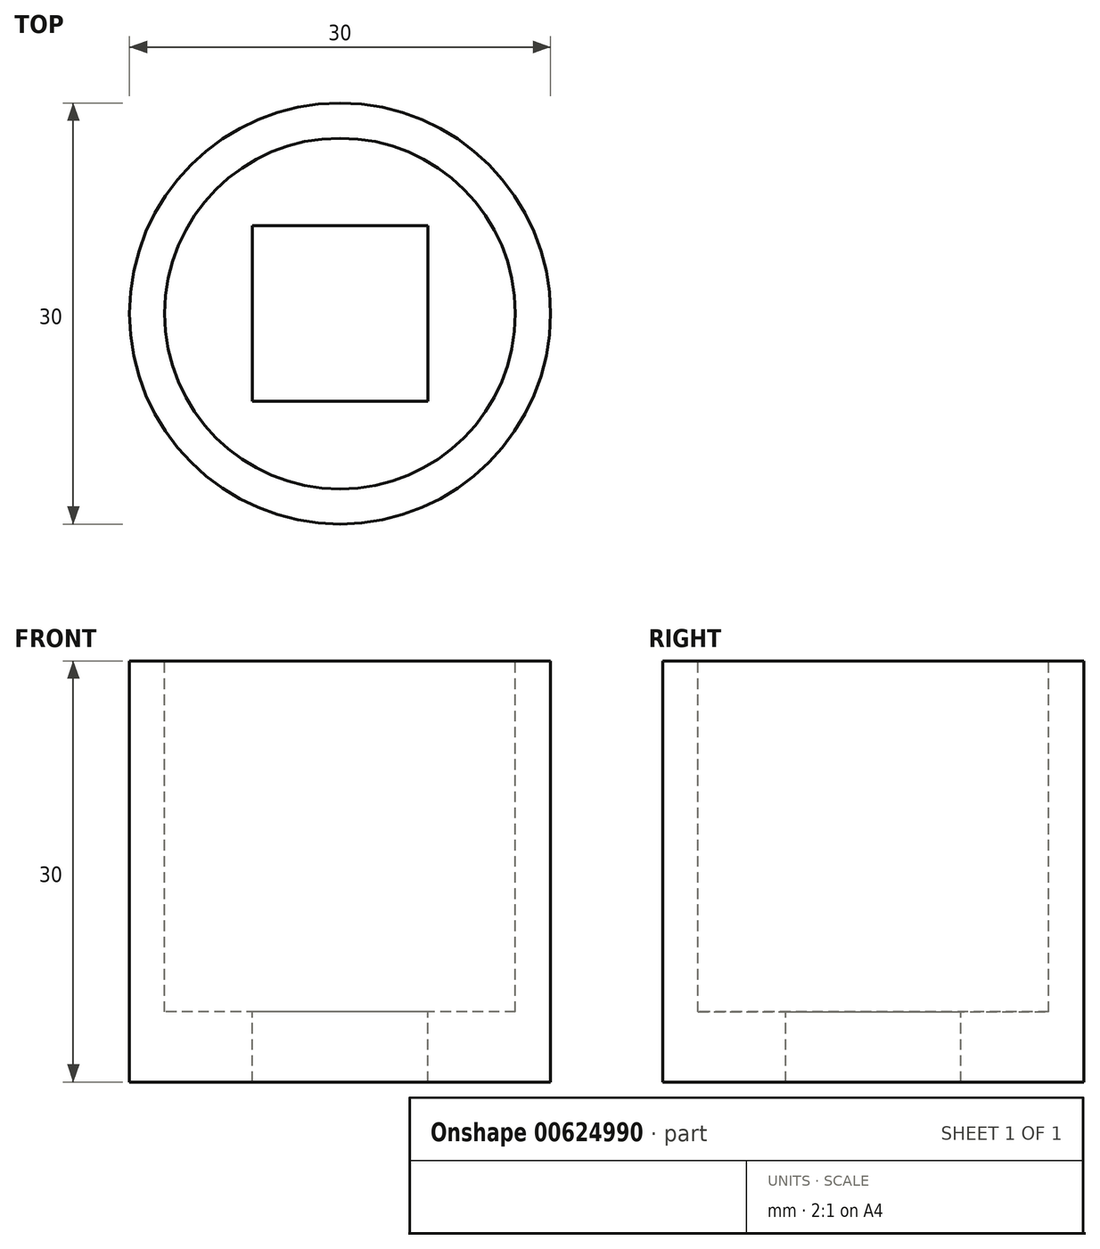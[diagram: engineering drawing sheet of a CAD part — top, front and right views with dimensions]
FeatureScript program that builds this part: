
annotation { "Feature Type Name" : "Feature", "Feature Type Description" : "" }
export const myFeature = defineFeature(function(context is Context, id is Id, definition is map)
    precondition{}
    {
        {
            var Q0;
            Q0=qCreatedBy(makeId("Top.planeOp"),FACE);
            var sketch = newSketch(context, id + "F0", { "sketchPlane" : qUnion([Q0])});
            skCircle(sketch, "E0", {"center": v(0, 0) * mm, "radius": 15 * mm});
            skSolve(sketch);
        }
        {
            var Q0;
            Q0=makeQuery(id+"F0.imprint","IMPRINT",FACE,{"disambiguationData":[TD([[makeQuery(id+"F0.imprint","IMPRINT",EDGE,{"derivedFrom":sQuery(id+"F0.wireOp",EDGE,"E0")}),1.0]])]});
            extrude(context, id + "F1", {"entities" : qUnion([Q0]), "depth" : 30 * mm, "offsetDistance" : 25 * mm});
        }
        {
            var Q0;
            Q0=makeQuery(id+"F1.opExtrude","CAP_FACE",FACE,{"disambiguationData":[OSD([sQuery(id+"F0.wireOp",EDGE,"E0")])],"isStart":false});
            var sketch = newSketch(context, id + "F2", { "sketchPlane" : qUnion([Q0])});
            skCircle(sketch, "E1", {"center": v(0, 0) * mm, "radius": 12.5 * mm});
            skSolve(sketch);
        }
        {
            var Q0;
            Q0=makeQuery(id+"F2.imprint","IMPRINT",FACE,{"disambiguationData":[TD([[makeQuery(id+"F2.imprint","IMPRINT",EDGE,{"derivedFrom":sQuery(id+"F2.wireOp",EDGE,"E1")}),1.0]])]});
            extrude(context, id + "F3", {"entities" : qUnion([Q0]), "operationType" : NewBodyOperationType.REMOVE, "oppositeDirection" : true, "depth" : 25 * mm, "offsetDistance" : 25 * mm});
        }
        {
            var Q0;
            Q0=makeQuery(id+"F3.boolean.opBoolean","COPY",FACE,{"derivedFrom":makeQuery(id+"F3.opExtrude","CAP_FACE",FACE,{"disambiguationData":[OSD([sQuery(id+"F2.wireOp",EDGE,"E1")])],"isStart":false})});
            var sketch = newSketch(context, id + "F4", { "sketchPlane" : qUnion([Q0])});
            skLineSegment(sketch, "E2.bottom", {"start": v(6.25, -6.25) * mm, "end": v(-6.25, -6.25) * mm});
            skLineSegment(sketch, "E2.top", {"start": v(6.25, 6.25) * mm, "end": v(-6.25, 6.25) * mm});
            skLineSegment(sketch, "E2.left", {"start": v(6.25, -6.25) * mm, "end": v(6.25, 6.25) * mm});
            skLineSegment(sketch, "E2.right", {"start": v(-6.25, -6.25) * mm, "end": v(-6.25, 6.25) * mm});
            skPoint(sketch, "E2.middle", {"position": v(0, 0) * mm});
            skSolve(sketch);
        }
        {
            var Q0;
            Q0=makeQuery(id+"F4.imprint","IMPRINT",FACE,{"disambiguationData":[TD([[makeQuery(id+"F4.imprint","IMPRINT",EDGE,{"derivedFrom":sQuery(id+"F4.wireOp",EDGE,"E2.bottom")}),-1.0]])]});
            extrude(context, id + "F5", {"entities" : qUnion([Q0]), "operationType" : NewBodyOperationType.REMOVE, "endBound" : BoundingType.THROUGH_ALL, "oppositeDirection" : true, "depth" : 25 * mm, "offsetDistance" : 25 * mm});
        }
    });
